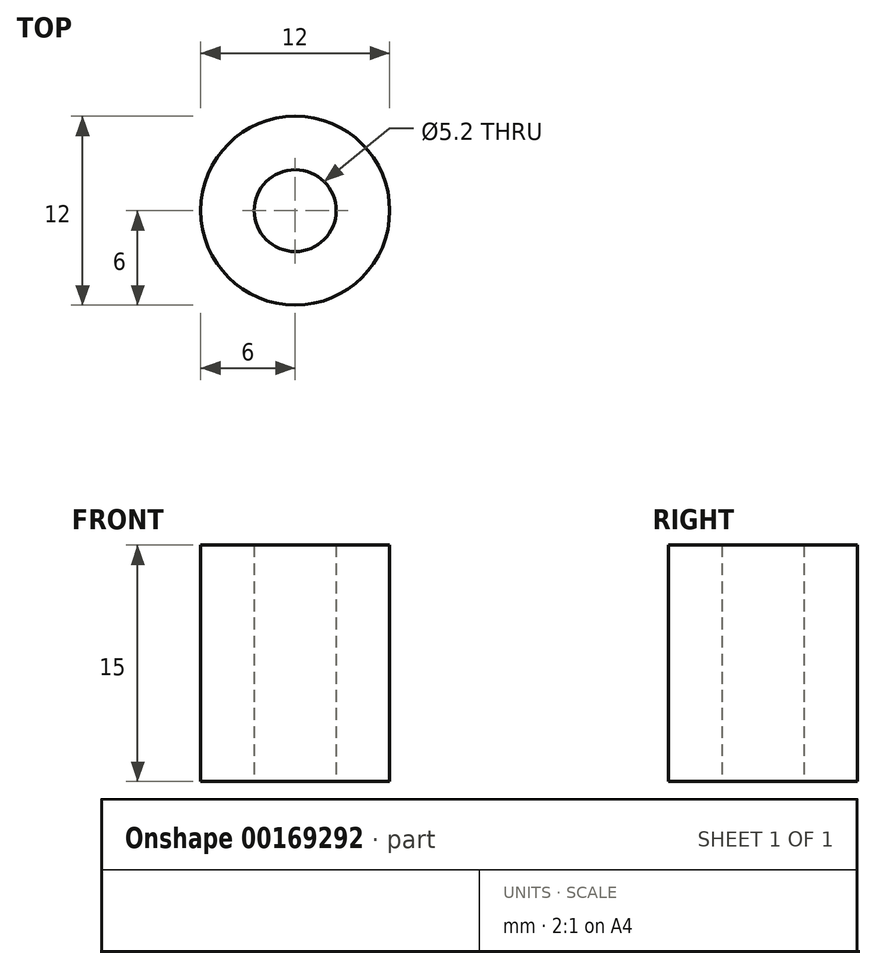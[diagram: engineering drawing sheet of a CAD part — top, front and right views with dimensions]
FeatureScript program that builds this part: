
annotation { "Feature Type Name" : "Feature", "Feature Type Description" : "" }
export const myFeature = defineFeature(function(context is Context, id is Id, definition is map)
    precondition{}
    {
        {
            var Q0;
            Q0=qCreatedBy(makeId("Top.planeOp"),FACE);
            var sketch = newSketch(context, id + "F0", { "sketchPlane" : qUnion([Q0])});
            skCircle(sketch, "E0", {"center": v(0, 0) * mm, "radius": 6 * mm});
            skCircle(sketch, "E1", {"center": v(0, 0) * mm, "radius": 2.6 * mm});
            skSolve(sketch);
        }
        {
            var Q0;
            Q0 = qSketchRegion(id + "F0", true);
            extrude(context, id + "F1", {"entities" : qUnion([Q0]), "depth" : 15 * mm});
        }
    });
